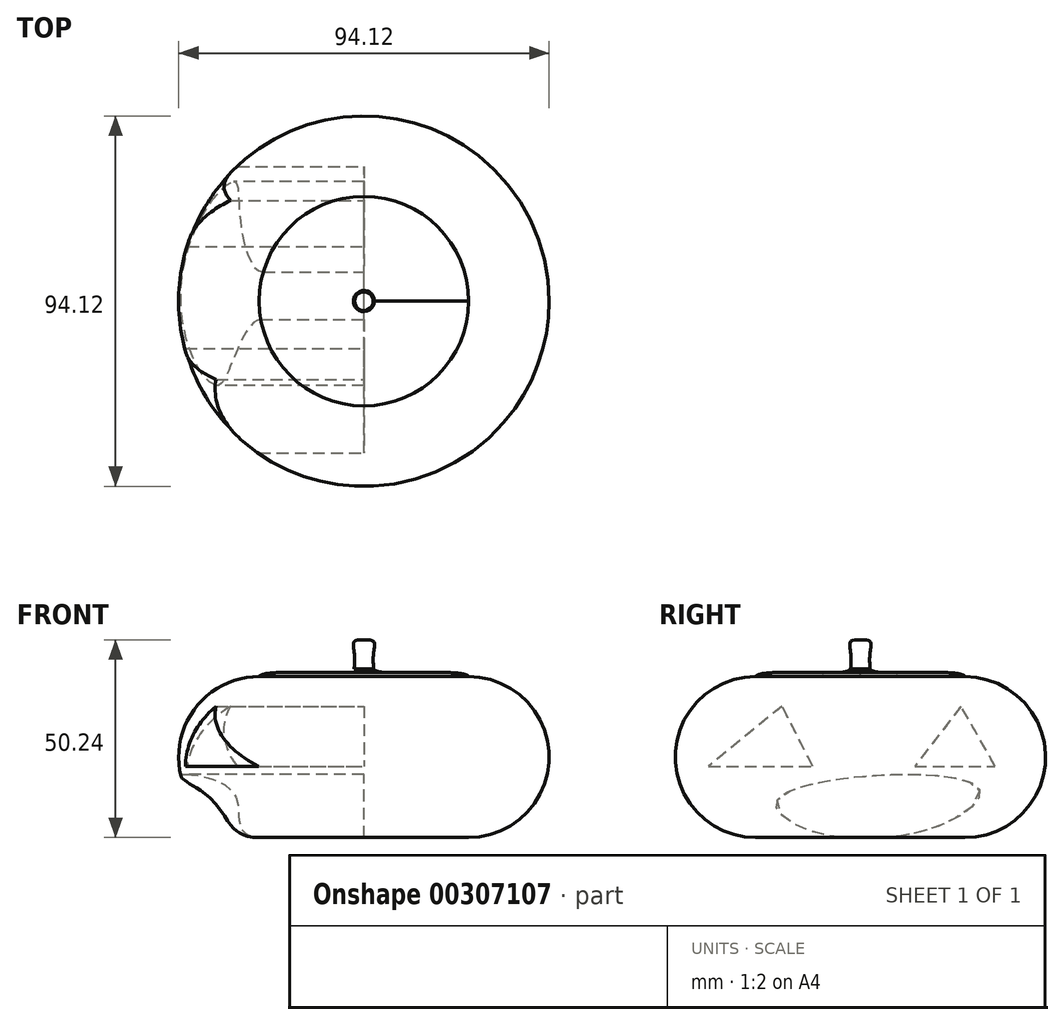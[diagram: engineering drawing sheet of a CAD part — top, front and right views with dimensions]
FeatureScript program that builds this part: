
annotation { "Feature Type Name" : "Feature", "Feature Type Description" : "" }
export const myFeature = defineFeature(function(context is Context, id is Id, definition is map)
    precondition{}
    {
        {
            var Q0;
            Q0=qCreatedBy(makeId("Front.planeOp"),FACE);
            var sketch = newSketch(context, id + "F0", { "sketchPlane" : qUnion([Q0])});
            skLineSegment(sketch, "E0", {"start": v(0, 0) * mm, "end": v(0, 121.72) * mm});
            skLineSegment(sketch, "E1", {"start": v(0, 121.72) * mm, "end": v(0, -90.82) * mm});
            skLineSegment(sketch, "E2", {"start": v(0, 0) * mm, "end": v(26.61, 0) * mm});
            skArc(sketch, "E3", {"start": v(26.61, 0) * mm, "mid": v(47.06, 20.45) * mm, "end": v(26.61, 40.9) * mm});
            skFitSpline(sketch, "E4", {"points": [v(26.61, 40.9) * mm, v(2.46, 42.83) * mm], "startDerivative": vector(-4.72, 7.35) * mm, "endDerivative": vector(-4.72, 7.35) * mm});
            skFitSpline(sketch, "E5", {"points": [v(2.46, 42.83) * mm, v(2.46, 46.93) * mm, v(2.46, 49.8) * mm, v(0, 50.21) * mm], "startDerivative": vector(-0.62, 10.68) * mm, "endDerivative": vector(-10.38, -0.47) * mm});
            skSolve(sketch);
        }
        {
            var Q0;
            {var subQ0=sQuery(id+"F0.wireOp",EDGE,"E2");Q0=makeQuery(id+"F0.imprint","IMPRINT",FACE,{"disambiguationData":[TD([[makeQuery(id+"F0.imprint","IMPRINT",EDGE,{"derivedFrom":subQ0}),1.0]])]});}
            var Q1;
            Q1=sQuery(id+"F0.wireOp",EDGE,"E1");
            revolve(context, id + "F1", {"entities" : qUnion([Q0]), "axis" : qUnion([Q1]), "revolveType" : RevolveType.FULL});
        }
        {
            var Q0;
            Q0=qCreatedBy(makeId("Right.planeOp"),FACE);
            var sketch = newSketch(context, id + "F2", { "sketchPlane" : qUnion([Q0])});
            skLineSegment(sketch, "E6", {"start": v(-38.57, 18.13) * mm, "end": v(-12.09, 18.13) * mm});
            skLineSegment(sketch, "E7", {"start": v(-12.09, 18.13) * mm, "end": v(-19.86, 33.39) * mm});
            skLineSegment(sketch, "E8", {"start": v(-19.86, 33.39) * mm, "end": v(-38.57, 18.13) * mm});
            skLineSegment(sketch, "E9", {"start": v(13.81, 18.13) * mm, "end": v(34.25, 18.13) * mm});
            skLineSegment(sketch, "E10", {"start": v(34.25, 18.13) * mm, "end": v(25.61, 33.39) * mm});
            skLineSegment(sketch, "E11", {"start": v(25.61, 33.39) * mm, "end": v(13.81, 18.13) * mm});
            skSolve(sketch);
        }
        {
            var Q0;
            Q0 = qSketchRegion(id + "F2", true);
            extrude(context, id + "F3", {"entities" : qUnion([Q0]), "operationType" : NewBodyOperationType.REMOVE, "oppositeDirection" : true, "depth" : 127 * mm});
        }
        {
            var Q0;
            Q0=qCreatedBy(makeId("Right.planeOp"),FACE);
            var sketch = newSketch(context, id + "F4", { "sketchPlane" : qUnion([Q0])});
            skFitSpline(sketch, "E12", {"points": [v(29.36, 13.24) * mm, v(21.87, 3.74) * mm, v(-14.4, 2.3) * mm, v(-20.43, 10.36) * mm, v(29.36, 13.24) * mm]});
            skSolve(sketch);
        }
        {
            var Q0;
            Q0 = qSketchRegion(id + "F4", true);
            extrude(context, id + "F5", {"entities" : qUnion([Q0]), "operationType" : NewBodyOperationType.REMOVE, "oppositeDirection" : true, "depth" : 50.8 * mm});
        }
    });
